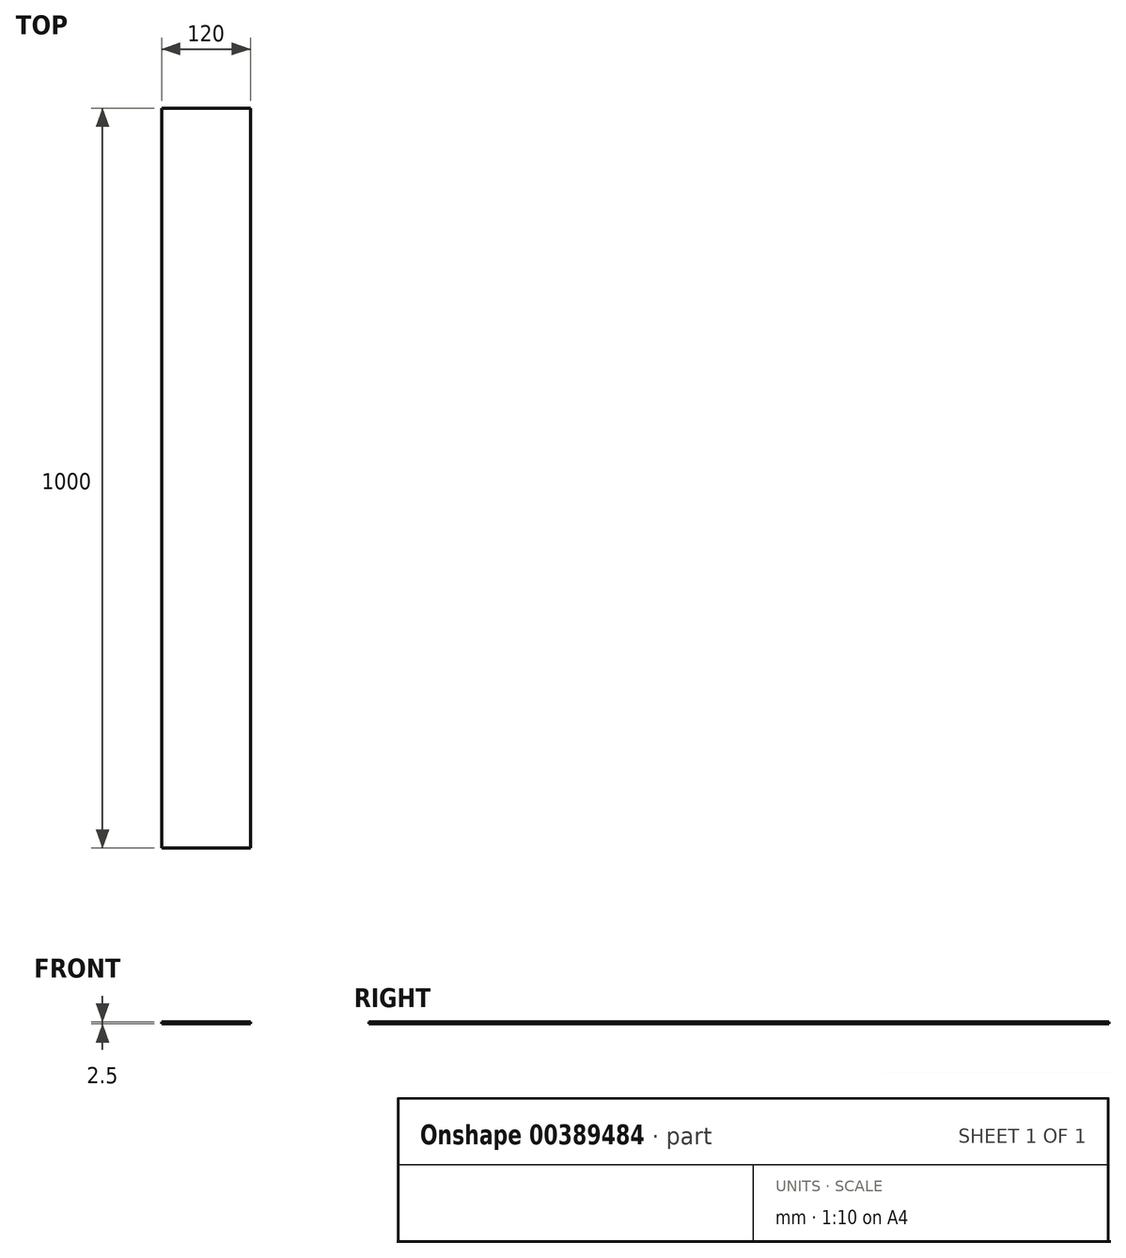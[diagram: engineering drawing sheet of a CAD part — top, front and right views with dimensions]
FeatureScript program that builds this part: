
annotation { "Feature Type Name" : "Feature", "Feature Type Description" : "" }
export const myFeature = defineFeature(function(context is Context, id is Id, definition is map)
    precondition{}
    {
        {
            var Q0;
            Q0=qCreatedBy(makeId("Front.planeOp"),FACE);
            var sketch = newSketch(context, id + "F0", { "sketchPlane" : qUnion([Q0])});
            skLineSegment(sketch, "E0.bottom", {"start": v(0, 0) * mm, "end": v(120, 0) * mm});
            skLineSegment(sketch, "E0.top", {"start": v(0, 2.5) * mm, "end": v(120, 2.5) * mm});
            skLineSegment(sketch, "E0.left", {"start": v(0, 0) * mm, "end": v(0, 2.5) * mm});
            skLineSegment(sketch, "E0.right", {"start": v(120, 0) * mm, "end": v(120, 2.5) * mm});
            skSolve(sketch);
        }
        {
            var Q0;
            Q0=makeQuery(id+"F0.imprint","IMPRINT",FACE,{"disambiguationData":[TD([[makeQuery(id+"F0.imprint","IMPRINT",EDGE,{"derivedFrom":sQuery(id+"F0.wireOp",EDGE,"E0.bottom")}),1.0]])]});
            extrude(context, id + "F1", {"entities" : qUnion([Q0]), "depth" : 1000 * mm});
        }
    });
